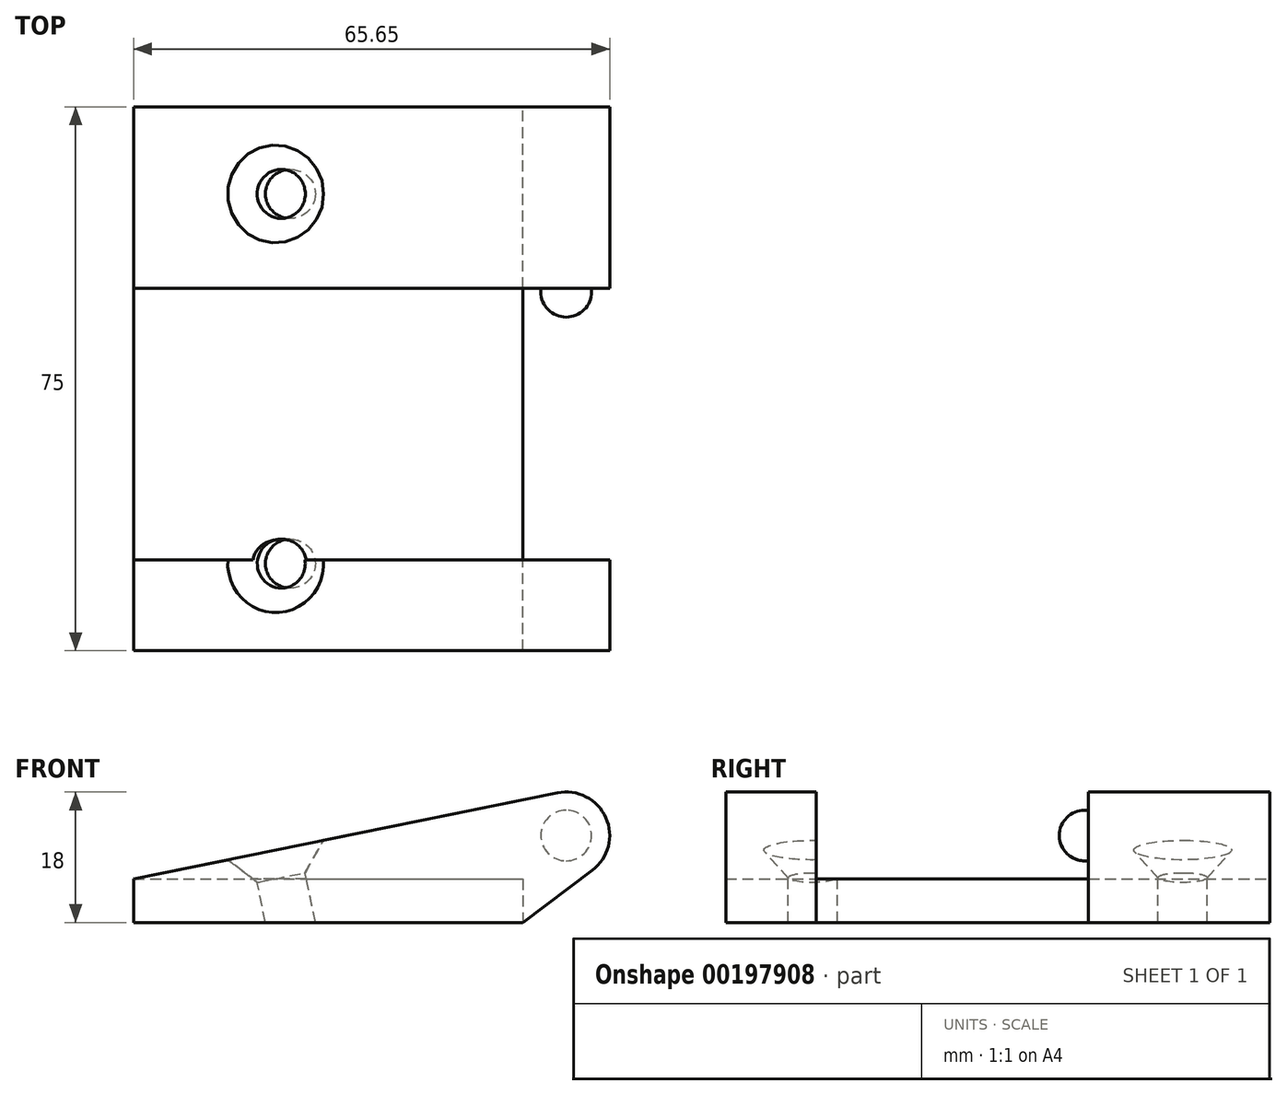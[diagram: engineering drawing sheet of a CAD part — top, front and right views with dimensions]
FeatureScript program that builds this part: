
annotation { "Feature Type Name" : "Feature", "Feature Type Description" : "" }
export const myFeature = defineFeature(function(context is Context, id is Id, definition is map)
    precondition{}
    {
        {
            var Q0;
            Q0=qCreatedBy(makeId("Front.planeOp"),FACE);
            var sketch = newSketch(context, id + "F0", { "sketchPlane" : qUnion([Q0])});
            skLineSegment(sketch, "E0", {"start": v(0, 0) * mm, "end": v(-53.65, 0) * mm});
            skLineSegment(sketch, "E1", {"start": v(-53.65, 0) * mm, "end": v(-53.65, 6) * mm});
            skLineSegment(sketch, "E2", {"start": v(-53.65, 6) * mm, "end": v(0, 6) * mm});
            skLineSegment(sketch, "E3", {"start": v(0, 6) * mm, "end": v(0, 0) * mm});
            skCircle(sketch, "E4", {"center": v(6, 12) * mm, "radius": 3 * mm});
            skCircle(sketch, "E5", {"center": v(6, 12) * mm, "radius": 6 * mm});
            skLineSegment(sketch, "E6", {"start": v(0, 0) * mm, "end": v(9.6, 7.2) * mm});
            skLineSegment(sketch, "E7", {"start": v(4.8, 17.88) * mm, "end": v(-53.65, 6) * mm});
            skSolve(sketch);
        }
        {
            var Q0;
            Q0=makeQuery(id+"F0.imprint","IMPRINT",FACE,{"disambiguationData":[TD([[makeQuery(id+"F0.imprint","IMPRINT",EDGE,{"derivedFrom":sQuery(id+"F0.wireOp",EDGE,"E0")}),-1.0]])]});
            var Q1;
            {var subQ0=sQuery(id+"F0.wireOp",EDGE,"E3");Q1=makeQuery(id+"F0.imprint","IMPRINT",FACE,{"disambiguationData":[TD([[makeQuery(id+"F0.imprint","IMPRINT",EDGE,{"derivedFrom":subQ0}),1.0]])]});}
            var Q2;
            Q2=makeQuery(id+"F0.imprint","IMPRINT",FACE,{"disambiguationData":[TD([[makeQuery(id+"F0.imprint","IMPRINT",EDGE,{"derivedFrom":sQuery(id+"F0.wireOp",EDGE,"E4")}),-1.0]])]});
            var Q3;
            Q3=makeQuery(id+"F0.imprint","IMPRINT",FACE,{"disambiguationData":[TD([[makeQuery(id+"F0.imprint","IMPRINT",EDGE,{"derivedFrom":sQuery(id+"F0.wireOp",EDGE,"E4")}),1.0]])]});
            var Q4;
            {var subQ0=sQuery(id+"F0.wireOp",EDGE,"E2");Q4=makeQuery(id+"F0.imprint","IMPRINT",FACE,{"disambiguationData":[TD([[makeQuery(id+"F0.imprint","IMPRINT",EDGE,{"derivedFrom":subQ0}),1.0]])]});}
            extrude(context, id + "F1", {"entities" : qUnion([Q0, Q1, Q2, Q3, Q4]), "depth" : 37.5 * mm, "hasSecondDirection" : true, "secondDirectionOppositeDirection" : true, "secondDirectionDepth" : 37.5 * mm});
        }
        {
            var Q0;
            Q0=makeQuery(id+"F1.opExtrude","CAP_FACE",FACE,{"disambiguationData":[OSD([sQuery(id+"F0.wireOp",EDGE,"E0"),sQuery(id+"F0.wireOp",EDGE,"E1"),sQuery(id+"F0.wireOp",EDGE,"E5"),sQuery(id+"F0.wireOp",EDGE,"E6"),sQuery(id+"F0.wireOp",EDGE,"E7")])],"isStart":false});
            var sketch = newSketch(context, id + "F2", { "sketchPlane" : qUnion([Q0])});
            skCircle(sketch, "E8.0", {"center": v(6, 12) * mm, "radius": 6 * mm});
            skLineSegment(sketch, "E8.1", {"start": v(-53.65, 6) * mm, "end": v(0, 6) * mm});
            skLineSegment(sketch, "E8.2", {"start": v(4.8, 17.88) * mm, "end": v(-53.65, 6) * mm});
            skLineSegment(sketch, "E9.0", {"start": v(0, 6) * mm, "end": v(0, 0) * mm});
            skSolve(sketch);
        }
        {
            var Q0;
            {var subQ0=sQuery(id+"F0.wireOp",EDGE,"E2");Q0=makeQuery(id+"F0.imprint","IMPRINT",FACE,{"disambiguationData":[TD([[makeQuery(id+"F0.imprint","IMPRINT",EDGE,{"derivedFrom":subQ0}),1.0]])]});}
            var Q1;
            Q1=makeQuery(id+"F0.imprint","IMPRINT",FACE,{"disambiguationData":[TD([[makeQuery(id+"F0.imprint","IMPRINT",EDGE,{"derivedFrom":sQuery(id+"F0.wireOp",EDGE,"E4")}),-1.0]])]});
            var Q2;
            Q2=makeQuery(id+"F0.imprint","IMPRINT",FACE,{"disambiguationData":[TD([[makeQuery(id+"F0.imprint","IMPRINT",EDGE,{"derivedFrom":sQuery(id+"F0.wireOp",EDGE,"E4")}),1.0]])]});
            var Q3;
            {var subQ0=sQuery(id+"F0.wireOp",EDGE,"E3");Q3=makeQuery(id+"F0.imprint","IMPRINT",FACE,{"disambiguationData":[TD([[makeQuery(id+"F0.imprint","IMPRINT",EDGE,{"derivedFrom":subQ0}),1.0]])]});}
            extrude(context, id + "F3", {"entities" : qUnion([Q0, Q1, Q2, Q3]), "operationType" : NewBodyOperationType.REMOVE, "depth" : 12.5 * mm, "hasSecondDirection" : true, "secondDirectionOppositeDirection" : true, "secondDirectionDepth" : 12.5 * mm});
        }
        {
            var Q0;
            Q0=makeQuery(id+"F3.boolean.opBoolean","COPY",FACE,{"derivedFrom":makeQuery(id+"F3.opExtrude","CAP_FACE",FACE,{"disambiguationData":[OSD([sQuery(id+"F0.wireOp",EDGE,"E2"),sQuery(id+"F0.wireOp",EDGE,"E3"),sQuery(id+"F0.wireOp",EDGE,"E5"),sQuery(id+"F0.wireOp",EDGE,"E6"),sQuery(id+"F0.wireOp",EDGE,"E7")])],"isStart":true})});
            var sketch = newSketch(context, id + "F4", { "sketchPlane" : qUnion([Q0])});
            skCircle(sketch, "E10", {"center": v(6, 12) * mm, "radius": 3.5 * mm});
            skSolve(sketch);
        }
        {
            var Q0;
            Q0=makeQuery(id+"F4.imprint","IMPRINT",FACE,{"disambiguationData":[TD([[makeQuery(id+"F4.imprint","IMPRINT",EDGE,{"derivedFrom":sQuery(id+"F4.wireOp",EDGE,"E10")}),1.0]])]});
            extrude(context, id + "F5", {"entities" : qUnion([Q0]), "operationType" : NewBodyOperationType.ADD, "depth" : 4 * mm});
        }
        {
            var Q0;
            Q0=makeQuery(id+"F3.boolean.opBoolean","COPY",FACE,{"derivedFrom":makeQuery(id+"F3.opExtrude","CAP_FACE",FACE,{"disambiguationData":[OSD([sQuery(id+"F0.wireOp",EDGE,"E2"),sQuery(id+"F0.wireOp",EDGE,"E3"),sQuery(id+"F0.wireOp",EDGE,"E5"),sQuery(id+"F0.wireOp",EDGE,"E6"),sQuery(id+"F0.wireOp",EDGE,"E7")])],"isStart":false})});
            var sketch = newSketch(context, id + "F6", { "sketchPlane" : qUnion([Q0])});
            skCircle(sketch, "E11", {"center": v(-6, 12) * mm, "radius": 3.5 * mm});
            skSolve(sketch);
        }
        {
            var Q0;
            Q0=makeQuery(id+"F6.imprint","IMPRINT",FACE,{"disambiguationData":[TD([[makeQuery(id+"F6.imprint","IMPRINT",EDGE,{"derivedFrom":sQuery(id+"F6.wireOp",EDGE,"E11")}),1.0]])]});
            extrude(context, id + "F7", {"entities" : qUnion([Q0]), "operationType" : NewBodyOperationType.ADD, "depth" : 4 * mm});
        }
        {
            var Q0;
            Q0=makeQuery(id+"F7.opExtrude","CAP_EDGE",EDGE,{"disambiguationData":[OSD([sQuery(id+"F6.wireOp",EDGE,"E11")])],"isStart":false});
            var Q1;
            Q1=makeQuery(id+"F5.opExtrude","CAP_EDGE",EDGE,{"disambiguationData":[OSD([sQuery(id+"F4.wireOp",EDGE,"E10")])],"isStart":false});
            fillet(context, id + "F8", {"entities" : qUnion([Q0, Q1]), "radius" : 3.5 * mm, "tangentPropagation" : true, "allowEdgeOverflow" : false});
        }
        {
            var Q0;
            {var subQ1=sQuery(id+"F0.wireOp",EDGE,"E5");var subQ2=sQuery(id+"F0.wireOp",EDGE,"E1");var subQ3=sQuery(id+"F0.wireOp",EDGE,"E7");var subQ4=sQuery(id+"F0.wireOp",EDGE,"E6");Q0=makeQuery(id+"F3.boolean.opBoolean","SPLIT",FACE,{"disambiguationData":[TD([makeQuery(id+"F1.opExtrude","CAP_FACE",FACE,{"disambiguationData":[OSD([sQuery(id+"F0.wireOp",EDGE,"E0"),subQ2,subQ1,subQ4,subQ3])],"isStart":false})])],"derivedFrom":makeQuery(id+"F1.opExtrude","SWEPT_FACE",FACE,{"disambiguationData":[OSD([subQ3])]})});}
            var sketch = newSketch(context, id + "F9", { "sketchPlane" : qUnion([Q0])});
            skPoint(sketch, "E12", {"position": v(-31.38, -25.5) * mm});
            skPoint(sketch, "E13", {"position": v(-31.38, 25.5) * mm});
            skSolve(sketch);
        }
        {
            var Q0;
            Q0=sQuery(id+"F9.wireOp",VERTEX,"E12");
            var Q1;
            Q1=sQuery(id+"F9.wireOp",VERTEX,"E13");
            var Q2;
            Q2=makeQuery(id+"F1.opExtrude","SWEPT_BODY",BODY,{"disambiguationData":[OSD([sQuery(id+"F0.wireOp",EDGE,"E0"),sQuery(id+"F0.wireOp",EDGE,"E1"),sQuery(id+"F0.wireOp",EDGE,"E5"),sQuery(id+"F0.wireOp",EDGE,"E6"),sQuery(id+"F0.wireOp",EDGE,"E7")])]});
            hole(context, id + "F10", {"style" : HoleStyle.C_SINK, "endStyle" : HoleEndStyle.THROUGH, "standardTappedOrClearance" : lookupTablePath({ "standard" : "ANSI", "fit" : "Normal (ASME)", "size" : "1/4", "type" : "Clearance" }), "standardBlindInLast" : lookupTablePath({ "fit" : "Free", "standard" : "ANSI", "size" : "1/4", "type" : "Clearance" }), "holeDiameter" : 6.76 * mm, "cSinkDiameter" : 13.5 * mm, "cSinkAngle" : 82 * degree, "startFromSketch" : true, "locations" : qUnion([Q0, Q1]), "scope" : qUnion([Q2]), "isTappedThrough" : true});
        }
        {
            var Q0;
            {var subQ0=sQuery(id+"F0.wireOp",EDGE,"E2");Q0=makeQuery(id+"F0.imprint","IMPRINT",FACE,{"disambiguationData":[TD([[makeQuery(id+"F0.imprint","IMPRINT",EDGE,{"derivedFrom":subQ0}),1.0]])]});}
            var Q1;
            Q1=makeQuery(id+"F0.imprint","IMPRINT",FACE,{"disambiguationData":[TD([[makeQuery(id+"F0.imprint","IMPRINT",EDGE,{"derivedFrom":sQuery(id+"F0.wireOp",EDGE,"E4")}),-1.0]])]});
            var Q2;
            Q2=makeQuery(id+"F0.imprint","IMPRINT",FACE,{"disambiguationData":[TD([[makeQuery(id+"F0.imprint","IMPRINT",EDGE,{"derivedFrom":sQuery(id+"F0.wireOp",EDGE,"E4")}),1.0]])]});
            var Q3;
            {var subQ0=sQuery(id+"F0.wireOp",EDGE,"E3");Q3=makeQuery(id+"F0.imprint","IMPRINT",FACE,{"disambiguationData":[TD([[makeQuery(id+"F0.imprint","IMPRINT",EDGE,{"derivedFrom":subQ0}),1.0]])]});}
            extrude(context, id + "F11", {"entities" : qUnion([Q0, Q1, Q2, Q3]), "operationType" : NewBodyOperationType.REMOVE, "depth" : 25 * mm});
        }
    });
